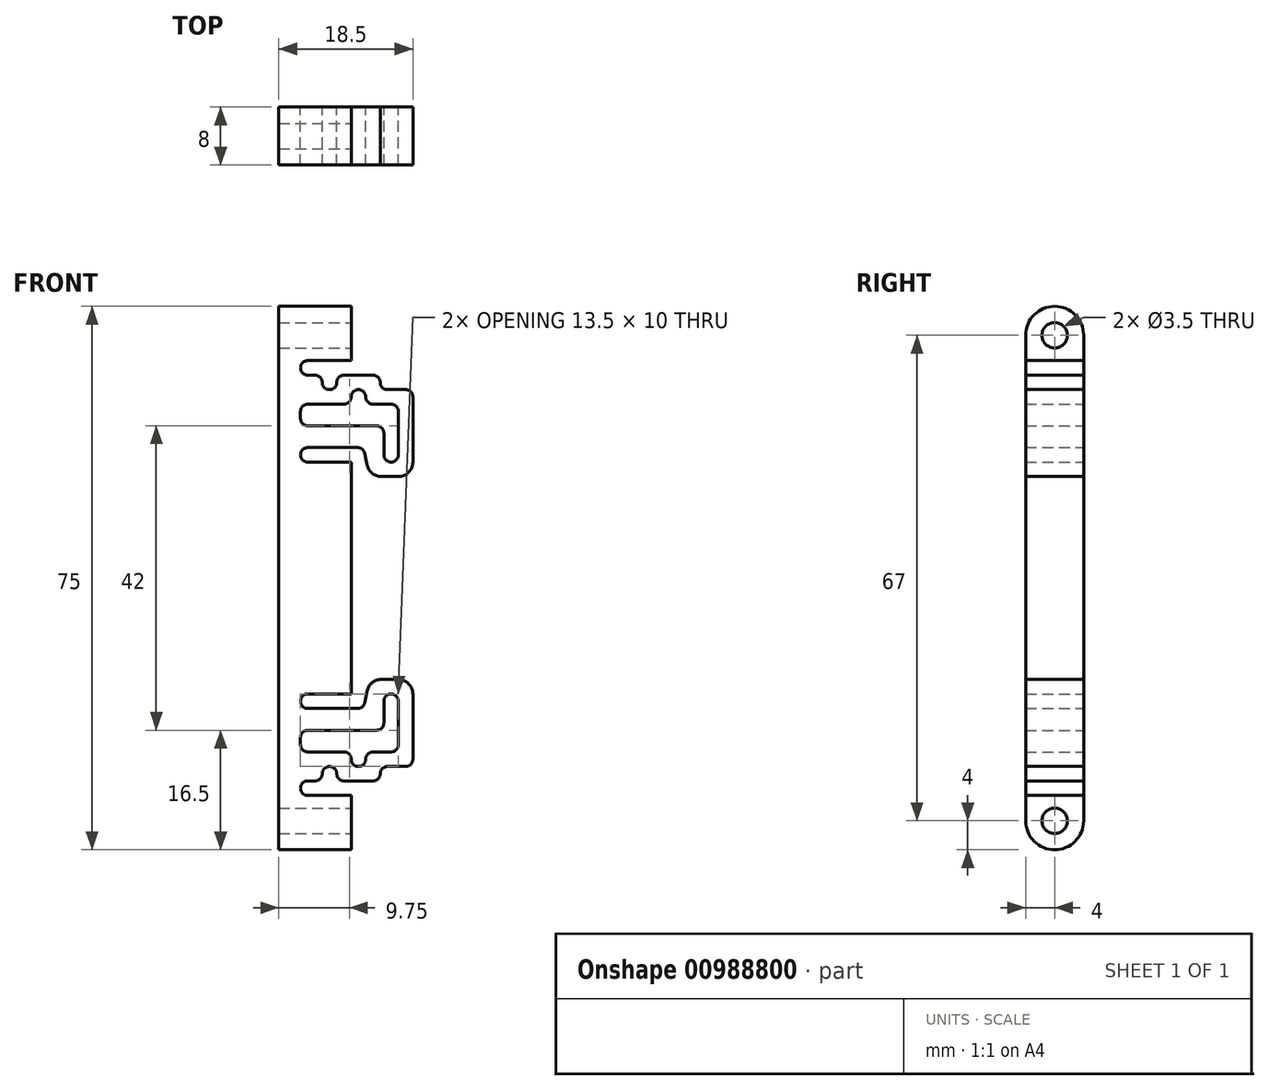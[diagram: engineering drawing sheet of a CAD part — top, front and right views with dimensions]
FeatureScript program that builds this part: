
annotation { "Feature Type Name" : "Feature", "Feature Type Description" : "" }
export const myFeature = defineFeature(function(context is Context, id is Id, definition is map)
    precondition{}
    {
        {
            var Q0;
            Q0=qCreatedBy(makeId("Front.planeOp"),FACE);
            var sketch = newSketch(context, id + "F0", { "sketchPlane" : qUnion([Q0])});
            skLineSegment(sketch, "E0.bottom", {"start": v(0, 0) * mm, "end": v(10, 0) * mm});
            skLineSegment(sketch, "E0.top", {"start": v(0, 75) * mm, "end": v(10, 75) * mm});
            skLineSegment(sketch, "E0.left", {"start": v(0, 0) * mm, "end": v(0, 75) * mm});
            skLineSegment(sketch, "E0.right", {"start": v(10, 0) * mm, "end": v(10, 75) * mm});
            skLineSegment(sketch, "E1", {"start": v(0, 37.5) * mm, "end": v(10, 37.5) * mm, "construction": true});
            skLineSegment(sketch, "E2.bottom", {"start": v(10, 55.5) * mm, "end": v(11.5, 55.5) * mm});
            skLineSegment(sketch, "E2.top", {"start": v(10, 19.5) * mm, "end": v(11.5, 19.5) * mm});
            skLineSegment(sketch, "E2.left", {"start": v(10, 55.5) * mm, "end": v(10, 19.5) * mm});
            skLineSegment(sketch, "E2.right", {"start": v(11.5, 55.5) * mm, "end": v(11.5, 19.5) * mm});
            skLineSegment(sketch, "E3.bottom", {"start": v(11.5, 51.5) * mm, "end": v(18.5, 51.5) * mm});
            skLineSegment(sketch, "E3.top", {"start": v(11.5, 23.5) * mm, "end": v(18.5, 23.5) * mm});
            skLineSegment(sketch, "E3.left", {"start": v(11.5, 51.5) * mm, "end": v(11.5, 23.5) * mm});
            skLineSegment(sketch, "E3.right", {"start": v(18.5, 51.5) * mm, "end": v(18.5, 23.5) * mm});
            skLineSegment(sketch, "E4.bottom", {"start": v(10, 75) * mm, "end": v(18.5, 75) * mm});
            skLineSegment(sketch, "E4.top", {"start": v(10, 0) * mm, "end": v(18.5, 0) * mm});
            skLineSegment(sketch, "E4.left", {"start": v(10, 75) * mm, "end": v(10, 0) * mm});
            skLineSegment(sketch, "E4.right", {"start": v(18.5, 75) * mm, "end": v(18.5, 0) * mm});
            skLineSegment(sketch, "E5.bottom", {"start": v(3, 61.5) * mm, "end": v(16.5, 61.5) * mm});
            skLineSegment(sketch, "E5.top", {"start": v(3, 58.5) * mm, "end": v(16.5, 58.5) * mm});
            skLineSegment(sketch, "E5.left", {"start": v(3, 61.5) * mm, "end": v(3, 58.5) * mm});
            skLineSegment(sketch, "E5.right", {"start": v(16.5, 61.5) * mm, "end": v(16.5, 58.5) * mm});
            skLineSegment(sketch, "E6.bottom", {"start": v(18.5, 75) * mm, "end": v(10, 75) * mm});
            skLineSegment(sketch, "E6.top", {"start": v(18.5, 65.5) * mm, "end": v(10, 65.5) * mm});
            skLineSegment(sketch, "E6.left", {"start": v(18.5, 75) * mm, "end": v(18.5, 65.5) * mm});
            skLineSegment(sketch, "E6.right", {"start": v(10, 75) * mm, "end": v(10, 65.5) * mm});
            skLineSegment(sketch, "E7.top", {"start": v(10, 9.5) * mm, "end": v(18.5, 9.5) * mm});
            skLineSegment(sketch, "E7.left", {"start": v(10, 0) * mm, "end": v(10, 9.5) * mm});
            skLineSegment(sketch, "E7.right", {"start": v(18.5, 0) * mm, "end": v(18.5, 9.5) * mm});
            skLineSegment(sketch, "E8.bottom", {"start": v(3, 16.5) * mm, "end": v(16.5, 16.5) * mm});
            skLineSegment(sketch, "E8.top", {"start": v(3, 13.5) * mm, "end": v(16.5, 13.5) * mm});
            skLineSegment(sketch, "E8.left", {"start": v(3, 16.5) * mm, "end": v(3, 13.5) * mm});
            skLineSegment(sketch, "E8.right", {"start": v(16.5, 16.5) * mm, "end": v(16.5, 13.5) * mm});
            skLineSegment(sketch, "E9.bottom", {"start": v(10, 13.5) * mm, "end": v(12, 13.5) * mm});
            skLineSegment(sketch, "E9.top", {"start": v(10, 11.5) * mm, "end": v(12, 11.5) * mm});
            skLineSegment(sketch, "E9.left", {"start": v(10, 13.5) * mm, "end": v(10, 11.5) * mm});
            skLineSegment(sketch, "E9.right", {"start": v(12, 13.5) * mm, "end": v(12, 11.5) * mm});
            skLineSegment(sketch, "E10.bottom", {"start": v(14, 9.5) * mm, "end": v(18.5, 9.5) * mm});
            skLineSegment(sketch, "E10.top", {"start": v(14, 11.5) * mm, "end": v(18.5, 11.5) * mm});
            skLineSegment(sketch, "E10.left", {"start": v(14, 9.5) * mm, "end": v(14, 11.5) * mm});
            skLineSegment(sketch, "E10.right", {"start": v(18.5, 9.5) * mm, "end": v(18.5, 11.5) * mm});
            skLineSegment(sketch, "E11.bottom", {"start": v(10, 61.5) * mm, "end": v(12, 61.5) * mm});
            skLineSegment(sketch, "E11.top", {"start": v(10, 63.5) * mm, "end": v(12, 63.5) * mm});
            skLineSegment(sketch, "E11.left", {"start": v(10, 61.5) * mm, "end": v(10, 63.5) * mm});
            skLineSegment(sketch, "E11.right", {"start": v(12, 61.5) * mm, "end": v(12, 63.5) * mm});
            skLineSegment(sketch, "E12.bottom", {"start": v(14, 65.5) * mm, "end": v(18.5, 65.5) * mm});
            skLineSegment(sketch, "E12.top", {"start": v(14, 63.5) * mm, "end": v(18.5, 63.5) * mm});
            skLineSegment(sketch, "E12.left", {"start": v(14, 65.5) * mm, "end": v(14, 63.5) * mm});
            skLineSegment(sketch, "E12.right", {"start": v(18.5, 65.5) * mm, "end": v(18.5, 63.5) * mm});
            skLineSegment(sketch, "E13.bottom", {"start": v(16.5, 58.5) * mm, "end": v(14.5, 58.5) * mm});
            skLineSegment(sketch, "E13.top", {"start": v(16.5, 53.5) * mm, "end": v(14.5, 53.5) * mm});
            skLineSegment(sketch, "E13.left", {"start": v(16.5, 58.5) * mm, "end": v(16.5, 53.5) * mm});
            skLineSegment(sketch, "E13.right", {"start": v(14.5, 58.5) * mm, "end": v(14.5, 53.5) * mm});
            skLineSegment(sketch, "E14.bottom", {"start": v(16.5, 16.5) * mm, "end": v(14.5, 16.5) * mm});
            skLineSegment(sketch, "E14.top", {"start": v(16.5, 21.5) * mm, "end": v(14.5, 21.5) * mm});
            skLineSegment(sketch, "E14.left", {"start": v(16.5, 16.5) * mm, "end": v(16.5, 21.5) * mm});
            skLineSegment(sketch, "E14.right", {"start": v(14.5, 16.5) * mm, "end": v(14.5, 21.5) * mm});
            skLineSegment(sketch, "E15.bottom", {"start": v(10, 19.5) * mm, "end": v(3, 19.5) * mm});
            skLineSegment(sketch, "E15.top", {"start": v(10, 21.5) * mm, "end": v(3, 21.5) * mm});
            skLineSegment(sketch, "E15.left", {"start": v(10, 19.5) * mm, "end": v(10, 21.5) * mm});
            skLineSegment(sketch, "E15.right", {"start": v(3, 19.5) * mm, "end": v(3, 21.5) * mm});
            skLineSegment(sketch, "E16.bottom", {"start": v(10, 55.5) * mm, "end": v(3, 55.5) * mm});
            skLineSegment(sketch, "E16.top", {"start": v(10, 53.5) * mm, "end": v(3, 53.5) * mm});
            skLineSegment(sketch, "E16.left", {"start": v(10, 55.5) * mm, "end": v(10, 53.5) * mm});
            skLineSegment(sketch, "E16.right", {"start": v(3, 55.5) * mm, "end": v(3, 53.5) * mm});
            skLineSegment(sketch, "E17.bottom", {"start": v(10, 65.5) * mm, "end": v(3, 65.5) * mm});
            skLineSegment(sketch, "E17.top", {"start": v(10, 67.5) * mm, "end": v(3, 67.5) * mm});
            skLineSegment(sketch, "E17.left", {"start": v(10, 65.5) * mm, "end": v(10, 67.5) * mm});
            skLineSegment(sketch, "E17.right", {"start": v(3, 65.5) * mm, "end": v(3, 67.5) * mm});
            skLineSegment(sketch, "E18.bottom", {"start": v(10, 9.5) * mm, "end": v(3, 9.5) * mm});
            skLineSegment(sketch, "E18.top", {"start": v(10, 7.5) * mm, "end": v(3, 7.5) * mm});
            skLineSegment(sketch, "E18.left", {"start": v(10, 9.5) * mm, "end": v(10, 7.5) * mm});
            skLineSegment(sketch, "E18.right", {"start": v(3, 9.5) * mm, "end": v(3, 7.5) * mm});
            skLineSegment(sketch, "E19.bottom", {"start": v(6, 65.5) * mm, "end": v(8, 65.5) * mm});
            skLineSegment(sketch, "E19.top", {"start": v(6, 63.5) * mm, "end": v(8, 63.5) * mm});
            skLineSegment(sketch, "E19.left", {"start": v(6, 65.5) * mm, "end": v(6, 63.5) * mm});
            skLineSegment(sketch, "E19.right", {"start": v(8, 65.5) * mm, "end": v(8, 63.5) * mm});
            skLineSegment(sketch, "E20.bottom", {"start": v(6, 9.5) * mm, "end": v(8, 9.5) * mm});
            skLineSegment(sketch, "E20.top", {"start": v(6, 11.5) * mm, "end": v(8, 11.5) * mm});
            skLineSegment(sketch, "E20.left", {"start": v(6, 9.5) * mm, "end": v(6, 11.5) * mm});
            skLineSegment(sketch, "E20.right", {"start": v(8, 9.5) * mm, "end": v(8, 11.5) * mm});
            skSolve(sketch);
        }
        {
            var Q0;
            {var subQ1=sQuery(id+"F0.wireOp",EDGE,"E2.bottom");Q0=makeQuery(id+"F0.imprint","IMPRINT",FACE,{"disambiguationData":[TD([[makeQuery(id+"F0.imprint","IMPRINT",EDGE,{"derivedFrom":subQ1}),1.0]])]});}
            var Q1;
            {var subQ10=sQuery(id+"F0.wireOp",EDGE,"E2.top");Q1=makeQuery(id+"F0.imprint","IMPRINT",FACE,{"disambiguationData":[TD([[makeQuery(id+"F0.imprint","IMPRINT",EDGE,{"derivedFrom":subQ10}),-1.0]])]});}
            var Q2;
            {var subQ23=sQuery(id+"F0.wireOp",EDGE,"E0.bottom");Q2=makeQuery(id+"F0.imprint","IMPRINT",FACE,{"disambiguationData":[TD([[makeQuery(id+"F0.imprint","IMPRINT",EDGE,{"derivedFrom":subQ23}),1.0]])]});}
            extrude(context, id + "F1", {"entities" : qUnion([Q0, Q1, Q2]), "depth" : 8 * mm, "offsetDistance" : 25 * mm});
        }
        {
            var Q0;
            Q0=makeQuery(id+"F1.opExtrude","SWEPT_EDGE",EDGE,{"disambiguationData":[OSD([sQuery(id+"F0.wireOp",EDGE,"E2.right"),sQuery(id+"F0.wireOp",EDGE,"E3.bottom")])]});
            chamfer(context, id + "F2", {"entities" : qUnion([Q0]), "chamferType" : ChamferType.TWO_OFFSETS, "width1" : 1 * mm, "oppositeDirection" : false, "width2" : 5 * mm, "tangentPropagation" : true});
        }
        {
            var Q0;
            Q0=makeQuery(id+"F1.opExtrude","SWEPT_EDGE",EDGE,{"disambiguationData":[OSD([sQuery(id+"F0.wireOp",EDGE,"E2.right"),sQuery(id+"F0.wireOp",EDGE,"E3.top")])]});
            chamfer(context, id + "F3", {"entities" : qUnion([Q0]), "chamferType" : ChamferType.TWO_OFFSETS, "width1" : 5 * mm, "oppositeDirection" : false, "width2" : 1 * mm, "tangentPropagation" : true});
        }
        {
            var Q0;
            {var subQ0=sQuery(id+"F0.wireOp",EDGE,"E3.bottom");Q0=makeQuery(id+"F2.opChamfer","BLEND_EDGE",EDGE,{"blendedFrom":[makeQuery(id+"F1.opExtrude","SWEPT_EDGE",EDGE,{"disambiguationData":[OSD([sQuery(id+"F0.wireOp",EDGE,"E2.right"),subQ0])]}),makeQuery(id+"F1.opExtrude","SWEPT_FACE",FACE,{"disambiguationData":[OSD([subQ0])]})],"blendedInto":[makeQuery(id+"F1.opExtrude","SWEPT_FACE",FACE,{"disambiguationData":[OSD([subQ0])]})]});}
            var Q1;
            {var subQ0=sQuery(id+"F0.wireOp",EDGE,"E3.top");Q1=makeQuery(id+"F3.opChamfer","BLEND_EDGE",EDGE,{"blendedFrom":[makeQuery(id+"F1.opExtrude","SWEPT_EDGE",EDGE,{"disambiguationData":[OSD([sQuery(id+"F0.wireOp",EDGE,"E2.right"),subQ0])]}),makeQuery(id+"F1.opExtrude","SWEPT_FACE",FACE,{"disambiguationData":[OSD([subQ0])]})],"blendedInto":[makeQuery(id+"F1.opExtrude","SWEPT_FACE",FACE,{"disambiguationData":[OSD([subQ0])]})]});}
            var Q2;
            Q2=makeQuery(id+"F1.opExtrude","SWEPT_EDGE",EDGE,{"disambiguationData":[OSD([sQuery(id+"F0.wireOp",EDGE,"E3.top"),sQuery(id+"F0.wireOp",EDGE,"E3.right"),sQuery(id+"F0.wireOp",EDGE,"E4.right")])]});
            var Q3;
            Q3=makeQuery(id+"F1.opExtrude","SWEPT_EDGE",EDGE,{"disambiguationData":[OSD([sQuery(id+"F0.wireOp",EDGE,"E3.bottom"),sQuery(id+"F0.wireOp",EDGE,"E3.right"),sQuery(id+"F0.wireOp",EDGE,"E4.right")])]});
            fillet(context, id + "F4", {"entities" : qUnion([Q0, Q1, Q2, Q3]), "radius" : 2 * mm, "tangentPropagation" : true, "allowEdgeOverflow" : false});
        }
        {
            var Q0;
            Q0=makeQuery(id+"F1.opExtrude","SWEPT_EDGE",EDGE,{"disambiguationData":[OSD([sQuery(id+"F0.wireOp",EDGE,"E13.top"),sQuery(id+"F0.wireOp",EDGE,"E13.right")])]});
            var Q1;
            Q1=makeQuery(id+"F1.opExtrude","SWEPT_EDGE",EDGE,{"disambiguationData":[OSD([sQuery(id+"F0.wireOp",EDGE,"E13.top"),sQuery(id+"F0.wireOp",EDGE,"E13.left")])]});
            var Q2;
            Q2=makeQuery(id+"F1.opExtrude","SWEPT_EDGE",EDGE,{"disambiguationData":[OSD([sQuery(id+"F0.wireOp",EDGE,"E5.bottom"),sQuery(id+"F0.wireOp",EDGE,"E5.right")])]});
            var Q3;
            Q3=makeQuery(id+"F1.opExtrude","SWEPT_EDGE",EDGE,{"disambiguationData":[OSD([sQuery(id+"F0.wireOp",EDGE,"E11.top"),sQuery(id+"F0.wireOp",EDGE,"E11.right")])]});
            var Q4;
            Q4=makeQuery(id+"F1.opExtrude","SWEPT_EDGE",EDGE,{"disambiguationData":[OSD([sQuery(id+"F0.wireOp",EDGE,"E0.right"),sQuery(id+"F0.wireOp",EDGE,"E11.top")])]});
            var Q5;
            Q5=makeQuery(id+"F1.opExtrude","SWEPT_EDGE",EDGE,{"disambiguationData":[OSD([sQuery(id+"F0.wireOp",EDGE,"E5.top"),sQuery(id+"F0.wireOp",EDGE,"E5.left")])]});
            var Q6;
            Q6=makeQuery(id+"F1.opExtrude","SWEPT_EDGE",EDGE,{"disambiguationData":[OSD([sQuery(id+"F0.wireOp",EDGE,"E5.bottom"),sQuery(id+"F0.wireOp",EDGE,"E5.left")])]});
            var Q7;
            Q7=makeQuery(id+"F1.opExtrude","SWEPT_EDGE",EDGE,{"disambiguationData":[OSD([sQuery(id+"F0.wireOp",EDGE,"E12.top"),sQuery(id+"F0.wireOp",EDGE,"E12.left")])]});
            var Q8;
            Q8=makeQuery(id+"F1.opExtrude","SWEPT_EDGE",EDGE,{"disambiguationData":[OSD([sQuery(id+"F0.wireOp",EDGE,"E6.top"),sQuery(id+"F0.wireOp",EDGE,"E12.left")])]});
            var Q9;
            Q9=makeQuery(id+"F1.opExtrude","SWEPT_EDGE",EDGE,{"disambiguationData":[OSD([sQuery(id+"F0.wireOp",EDGE,"E4.right"),sQuery(id+"F0.wireOp",EDGE,"E12.top")])]});
            var Q10;
            Q10=makeQuery(id+"F1.opExtrude","SWEPT_EDGE",EDGE,{"disambiguationData":[OSD([sQuery(id+"F0.wireOp",EDGE,"E14.top"),sQuery(id+"F0.wireOp",EDGE,"E14.left")])]});
            var Q11;
            Q11=makeQuery(id+"F1.opExtrude","SWEPT_EDGE",EDGE,{"disambiguationData":[OSD([sQuery(id+"F0.wireOp",EDGE,"E14.top"),sQuery(id+"F0.wireOp",EDGE,"E14.right")])]});
            var Q12;
            Q12=makeQuery(id+"F1.opExtrude","SWEPT_EDGE",EDGE,{"disambiguationData":[OSD([sQuery(id+"F0.wireOp",EDGE,"E8.bottom"),sQuery(id+"F0.wireOp",EDGE,"E14.right")])]});
            var Q13;
            Q13=makeQuery(id+"F1.opExtrude","SWEPT_EDGE",EDGE,{"disambiguationData":[OSD([sQuery(id+"F0.wireOp",EDGE,"E8.top"),sQuery(id+"F0.wireOp",EDGE,"E8.right")])]});
            var Q14;
            Q14=makeQuery(id+"F1.opExtrude","SWEPT_EDGE",EDGE,{"disambiguationData":[OSD([sQuery(id+"F0.wireOp",EDGE,"E8.top"),sQuery(id+"F0.wireOp",EDGE,"E9.right")])]});
            var Q15;
            Q15=makeQuery(id+"F1.opExtrude","SWEPT_EDGE",EDGE,{"disambiguationData":[OSD([sQuery(id+"F0.wireOp",EDGE,"E9.top"),sQuery(id+"F0.wireOp",EDGE,"E9.right")])]});
            var Q16;
            Q16=makeQuery(id+"F1.opExtrude","SWEPT_EDGE",EDGE,{"disambiguationData":[OSD([sQuery(id+"F0.wireOp",EDGE,"E0.right"),sQuery(id+"F0.wireOp",EDGE,"E9.top")])]});
            var Q17;
            Q17=makeQuery(id+"F1.opExtrude","SWEPT_EDGE",EDGE,{"disambiguationData":[OSD([sQuery(id+"F0.wireOp",EDGE,"E0.right"),sQuery(id+"F0.wireOp",EDGE,"E8.top")])]});
            var Q18;
            Q18=makeQuery(id+"F1.opExtrude","SWEPT_EDGE",EDGE,{"disambiguationData":[OSD([sQuery(id+"F0.wireOp",EDGE,"E8.top"),sQuery(id+"F0.wireOp",EDGE,"E8.left")])]});
            var Q19;
            Q19=makeQuery(id+"F1.opExtrude","SWEPT_EDGE",EDGE,{"disambiguationData":[OSD([sQuery(id+"F0.wireOp",EDGE,"E8.bottom"),sQuery(id+"F0.wireOp",EDGE,"E8.left")])]});
            var Q20;
            Q20=makeQuery(id+"F1.opExtrude","SWEPT_EDGE",EDGE,{"disambiguationData":[OSD([sQuery(id+"F0.wireOp",EDGE,"E4.right"),sQuery(id+"F0.wireOp",EDGE,"E10.top")])]});
            var Q21;
            Q21=makeQuery(id+"F1.opExtrude","SWEPT_EDGE",EDGE,{"disambiguationData":[OSD([sQuery(id+"F0.wireOp",EDGE,"E10.top"),sQuery(id+"F0.wireOp",EDGE,"E10.left")])]});
            var Q22;
            Q22=makeQuery(id+"F1.opExtrude","SWEPT_EDGE",EDGE,{"disambiguationData":[OSD([sQuery(id+"F0.wireOp",EDGE,"E7.top"),sQuery(id+"F0.wireOp",EDGE,"E10.left")])]});
            var Q23;
            Q23=makeQuery(id+"F1.opExtrude","SWEPT_EDGE",EDGE,{"disambiguationData":[OSD([sQuery(id+"F0.wireOp",EDGE,"E5.bottom"),sQuery(id+"F0.wireOp",EDGE,"E11.right")])]});
            var Q24;
            Q24=makeQuery(id+"F1.opExtrude","SWEPT_EDGE",EDGE,{"disambiguationData":[OSD([sQuery(id+"F0.wireOp",EDGE,"E0.right"),sQuery(id+"F0.wireOp",EDGE,"E5.bottom")])]});
            var Q25;
            Q25=makeQuery(id+"F1.opExtrude","SWEPT_EDGE",EDGE,{"disambiguationData":[OSD([sQuery(id+"F0.wireOp",EDGE,"E5.top"),sQuery(id+"F0.wireOp",EDGE,"E13.right")])]});
            var Q26;
            Q26=makeQuery(id+"F1.opExtrude","SWEPT_EDGE",EDGE,{"disambiguationData":[OSD([sQuery(id+"F0.wireOp",EDGE,"E20.top"),sQuery(id+"F0.wireOp",EDGE,"E20.left")])]});
            var Q27;
            Q27=makeQuery(id+"F1.opExtrude","SWEPT_EDGE",EDGE,{"disambiguationData":[OSD([sQuery(id+"F0.wireOp",EDGE,"E18.bottom"),sQuery(id+"F0.wireOp",EDGE,"E20.left")])]});
            var Q28;
            Q28=makeQuery(id+"F1.opExtrude","SWEPT_EDGE",EDGE,{"disambiguationData":[OSD([sQuery(id+"F0.wireOp",EDGE,"E18.bottom"),sQuery(id+"F0.wireOp",EDGE,"E18.right")])]});
            var Q29;
            Q29=makeQuery(id+"F1.opExtrude","SWEPT_EDGE",EDGE,{"disambiguationData":[OSD([sQuery(id+"F0.wireOp",EDGE,"E20.top"),sQuery(id+"F0.wireOp",EDGE,"E20.right")])]});
            var Q30;
            Q30=makeQuery(id+"F1.opExtrude","SWEPT_EDGE",EDGE,{"disambiguationData":[OSD([sQuery(id+"F0.wireOp",EDGE,"E18.bottom"),sQuery(id+"F0.wireOp",EDGE,"E20.right")])]});
            var Q31;
            Q31=makeQuery(id+"F1.opExtrude","SWEPT_EDGE",EDGE,{"disambiguationData":[OSD([sQuery(id+"F0.wireOp",EDGE,"E18.top"),sQuery(id+"F0.wireOp",EDGE,"E18.right")])]});
            var Q32;
            Q32=makeQuery(id+"F1.opExtrude","SWEPT_EDGE",EDGE,{"disambiguationData":[OSD([sQuery(id+"F0.wireOp",EDGE,"E17.bottom"),sQuery(id+"F0.wireOp",EDGE,"E19.left")])]});
            var Q33;
            Q33=makeQuery(id+"F1.opExtrude","SWEPT_EDGE",EDGE,{"disambiguationData":[OSD([sQuery(id+"F0.wireOp",EDGE,"E17.bottom"),sQuery(id+"F0.wireOp",EDGE,"E19.right")])]});
            var Q34;
            Q34=makeQuery(id+"F1.opExtrude","SWEPT_EDGE",EDGE,{"disambiguationData":[OSD([sQuery(id+"F0.wireOp",EDGE,"E19.top"),sQuery(id+"F0.wireOp",EDGE,"E19.right")])]});
            var Q35;
            Q35=makeQuery(id+"F1.opExtrude","SWEPT_EDGE",EDGE,{"disambiguationData":[OSD([sQuery(id+"F0.wireOp",EDGE,"E19.top"),sQuery(id+"F0.wireOp",EDGE,"E19.left")])]});
            var Q36;
            Q36=makeQuery(id+"F1.opExtrude","SWEPT_EDGE",EDGE,{"disambiguationData":[OSD([sQuery(id+"F0.wireOp",EDGE,"E17.bottom"),sQuery(id+"F0.wireOp",EDGE,"E17.right")])]});
            var Q37;
            Q37=makeQuery(id+"F1.opExtrude","SWEPT_EDGE",EDGE,{"disambiguationData":[OSD([sQuery(id+"F0.wireOp",EDGE,"E17.top"),sQuery(id+"F0.wireOp",EDGE,"E17.right")])]});
            var Q38;
            Q38=makeQuery(id+"F1.opExtrude","SWEPT_EDGE",EDGE,{"disambiguationData":[OSD([sQuery(id+"F0.wireOp",EDGE,"E16.bottom"),sQuery(id+"F0.wireOp",EDGE,"E16.right")])]});
            var Q39;
            Q39=makeQuery(id+"F1.opExtrude","SWEPT_EDGE",EDGE,{"disambiguationData":[OSD([sQuery(id+"F0.wireOp",EDGE,"E16.top"),sQuery(id+"F0.wireOp",EDGE,"E16.right")])]});
            var Q40;
            Q40=makeQuery(id+"F2.opChamfer","BLEND_EDGE",EDGE,{"blendedFrom":[makeQuery(id+"F1.opExtrude","SWEPT_EDGE",EDGE,{"disambiguationData":[OSD([sQuery(id+"F0.wireOp",EDGE,"E2.right"),sQuery(id+"F0.wireOp",EDGE,"E3.bottom")])]}),makeQuery(id+"F1.opExtrude","SWEPT_FACE",FACE,{"disambiguationData":[OSD([sQuery(id+"F0.wireOp",EDGE,"E2.bottom"),sQuery(id+"F0.wireOp",EDGE,"E16.bottom")])]})],"blendedInto":[makeQuery(id+"F1.opExtrude","SWEPT_FACE",FACE,{"disambiguationData":[OSD([sQuery(id+"F0.wireOp",EDGE,"E2.bottom"),sQuery(id+"F0.wireOp",EDGE,"E16.bottom")])]})]});
            var Q41;
            Q41=makeQuery(id+"F3.opChamfer","BLEND_EDGE",EDGE,{"blendedFrom":[makeQuery(id+"F1.opExtrude","SWEPT_EDGE",EDGE,{"disambiguationData":[OSD([sQuery(id+"F0.wireOp",EDGE,"E2.right"),sQuery(id+"F0.wireOp",EDGE,"E3.top")])]}),makeQuery(id+"F1.opExtrude","SWEPT_FACE",FACE,{"disambiguationData":[OSD([sQuery(id+"F0.wireOp",EDGE,"E2.top"),sQuery(id+"F0.wireOp",EDGE,"E15.bottom")])]})],"blendedInto":[makeQuery(id+"F1.opExtrude","SWEPT_FACE",FACE,{"disambiguationData":[OSD([sQuery(id+"F0.wireOp",EDGE,"E2.top"),sQuery(id+"F0.wireOp",EDGE,"E15.bottom")])]})]});
            var Q42;
            Q42=makeQuery(id+"F1.opExtrude","SWEPT_EDGE",EDGE,{"disambiguationData":[OSD([sQuery(id+"F0.wireOp",EDGE,"E15.top"),sQuery(id+"F0.wireOp",EDGE,"E15.right")])]});
            var Q43;
            Q43=makeQuery(id+"F1.opExtrude","SWEPT_EDGE",EDGE,{"disambiguationData":[OSD([sQuery(id+"F0.wireOp",EDGE,"E15.bottom"),sQuery(id+"F0.wireOp",EDGE,"E15.right")])]});
            fillet(context, id + "F5", {"entities" : qUnion([Q0, Q1, Q2, Q3, Q4, Q5, Q6, Q7, Q8, Q9, Q10, Q11, Q12, Q13, Q14, Q15, Q16, Q17, Q18, Q19, Q20, Q21, Q22, Q23, Q24, Q25, Q26, Q27, Q28, Q29, Q30, Q31, Q32, Q33, Q34, Q35, Q36, Q37, Q38, Q39, Q40, Q41, Q42, Q43]), "radius" : 1 * mm, "tangentPropagation" : true, "allowEdgeOverflow" : false});
        }
        {
            var Q0;
            Q0=makeQuery(id+"F1.opExtrude","CAP_EDGE",EDGE,{"disambiguationData":[OSD([sQuery(id+"F0.wireOp",EDGE,"E0.top")])],"isStart":false});
            var Q1;
            Q1=makeQuery(id+"F1.opExtrude","CAP_EDGE",EDGE,{"disambiguationData":[OSD([sQuery(id+"F0.wireOp",EDGE,"E0.top")])],"isStart":true});
            var Q2;
            Q2=makeQuery(id+"F1.opExtrude","CAP_EDGE",EDGE,{"disambiguationData":[OSD([sQuery(id+"F0.wireOp",EDGE,"E0.bottom")])],"isStart":false});
            var Q3;
            Q3=makeQuery(id+"F1.opExtrude","CAP_EDGE",EDGE,{"disambiguationData":[OSD([sQuery(id+"F0.wireOp",EDGE,"E0.bottom")])],"isStart":true});
            fillet(context, id + "F6", {"entities" : qUnion([Q0, Q1, Q2, Q3]), "radius" : 4 * mm, "tangentPropagation" : true, "allowEdgeOverflow" : false});
        }
        {
            var Q0;
            {var subQ0=sQuery(id+"F0.wireOp",EDGE,"E0.right");Q0=makeQuery(id+"F1.opExtrude","SWEPT_FACE",FACE,{"disambiguationData":[OSD([subQ0]),TDD([makeQuery(id+"F0.imprint","IMPRINT",EDGE,{"disambiguationData":[TD([[makeQuery(id+"F0.imprint","INTERSECT",VERTEX,{"derivedFrom":[subQ0,sQuery(id+"F0.wireOp",EDGE,"E17.top")]}),-1.0]])],"derivedFrom":subQ0})])]});}
            var sketch = newSketch(context, id + "F7", { "sketchPlane" : qUnion([Q0])});
            skLineSegment(sketch, "E21", {"start": v(-8, 71) * mm, "end": v(0, 71) * mm, "construction": true});
            skCircle(sketch, "E22", {"center": v(-4, 71) * mm, "radius": 1.75 * mm});
            skSolve(sketch);
        }
        {
            var Q0;
            Q0=makeQuery(id+"F7.imprint","IMPRINT",FACE,{"disambiguationData":[TD([[makeQuery(id+"F7.imprint","IMPRINT",EDGE,{"derivedFrom":sQuery(id+"F7.wireOp",EDGE,"E22")}),1.0]])]});
            var Q1;
            Q1=sQuery(id+"F7.wireOp",EDGE,"E22");
            extrude(context, id + "F8", {"entities" : qUnion([Q0]), "operationType" : NewBodyOperationType.REMOVE, "surfaceEntities" : qUnion([Q1]), "oppositeDirection" : true, "depth" : 10 * mm, "offsetDistance" : 25 * mm});
        }
        {
            var Q0;
            {var subQ0=sQuery(id+"F0.wireOp",EDGE,"E0.right");Q0=makeQuery(id+"F1.opExtrude","SWEPT_FACE",FACE,{"disambiguationData":[OSD([subQ0]),TDD([makeQuery(id+"F0.imprint","IMPRINT",EDGE,{"disambiguationData":[TD([[makeQuery(id+"F0.imprint","INTERSECT",VERTEX,{"derivedFrom":[subQ0,sQuery(id+"F0.wireOp",EDGE,"E18.top")]}),1.0]])],"derivedFrom":subQ0})])]});}
            var sketch = newSketch(context, id + "F9", { "sketchPlane" : qUnion([Q0])});
            skLineSegment(sketch, "E23", {"start": v(0, 4) * mm, "end": v(-8, 4) * mm, "construction": true});
            skCircle(sketch, "E24", {"center": v(-4, 4) * mm, "radius": 1.75 * mm});
            skPoint(sketch, "E24.perimeterSnap0", {"position": v(-4, 4) * mm});
            skPoint(sketch, "E24.perimeterSnap1", {"position": v(-8, 5.75) * mm});
            skSolve(sketch);
        }
        {
            var Q0;
            Q0=qSketchRegion(id+"F9",true);
            extrude(context, id + "F10", {"entities" : qUnion([Q0]), "operationType" : NewBodyOperationType.REMOVE, "oppositeDirection" : true, "depth" : 10 * mm, "offsetDistance" : 25 * mm});
        }
    });
